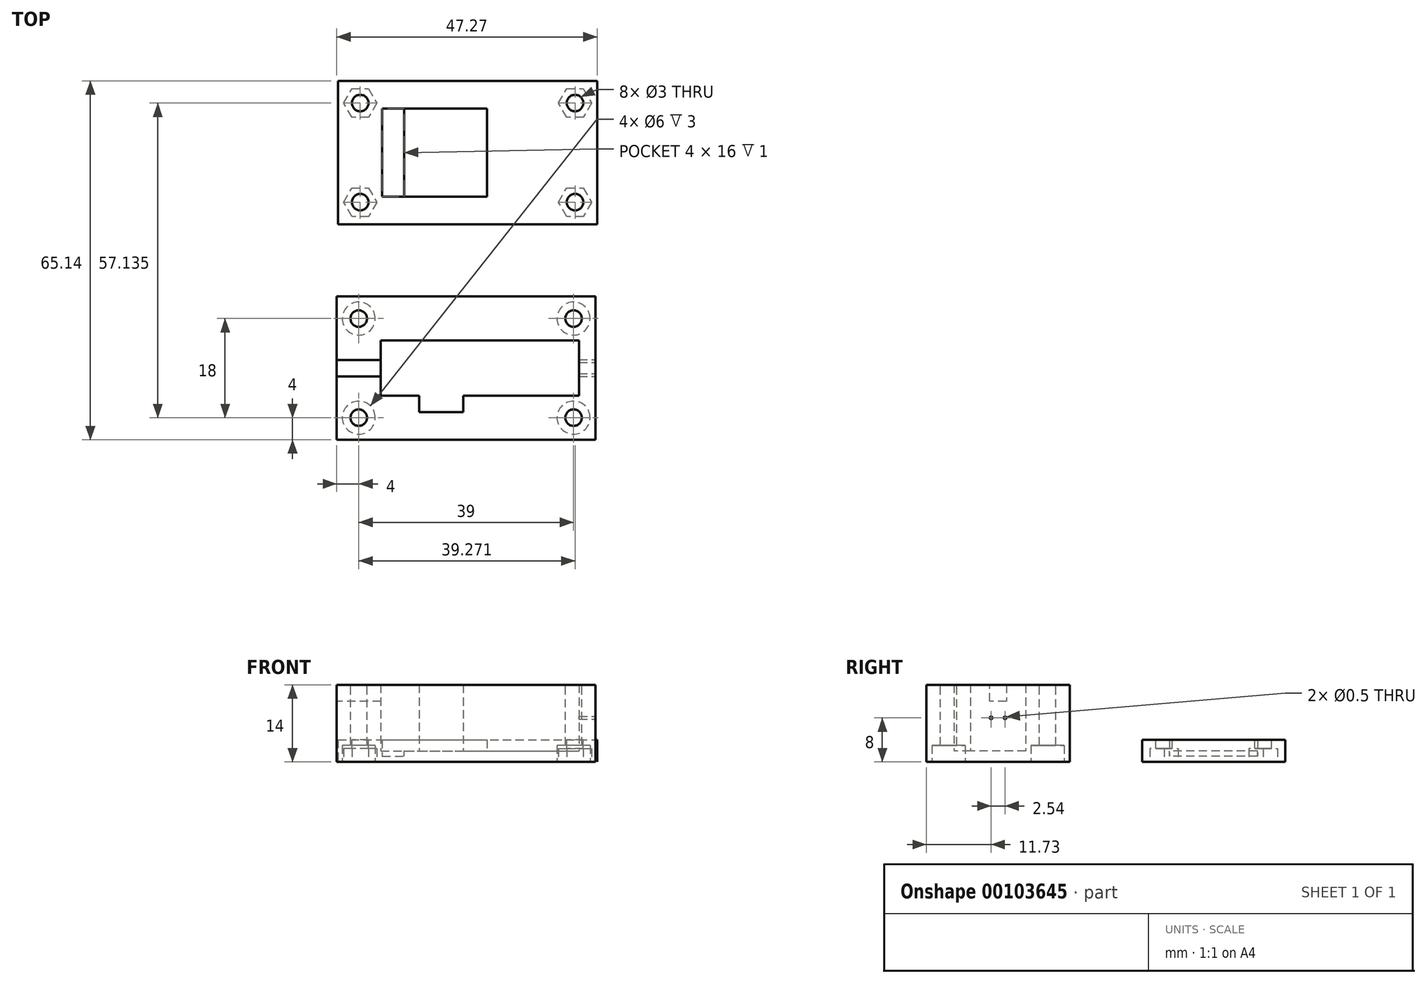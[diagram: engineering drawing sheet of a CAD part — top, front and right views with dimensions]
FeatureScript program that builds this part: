
annotation { "Feature Type Name" : "Feature", "Feature Type Description" : "" }
export const myFeature = defineFeature(function(context is Context, id is Id, definition is map)
    precondition{}
    {
        {
            var Q0;
            Q0=qCreatedBy(makeId("Top.planeOp"),FACE);
            var sketch = newSketch(context, id + "F0", { "sketchPlane" : qUnion([Q0])});
            skLineSegment(sketch, "E0.bottom", {"start": v(-10.35, 7.99) * mm, "end": v(8.65, 7.99) * mm});
            skLineSegment(sketch, "E0.top", {"start": v(-10.35, -8.01) * mm, "end": v(8.65, -8.01) * mm});
            skLineSegment(sketch, "E0.left", {"start": v(-10.35, 7.99) * mm, "end": v(-10.35, -8.01) * mm});
            skLineSegment(sketch, "E0.right", {"start": v(8.65, 7.99) * mm, "end": v(8.65, -8.01) * mm});
            skLineSegment(sketch, "E1.bottom", {"start": v(8.65, 7.99) * mm, "end": v(28.65, 7.99) * mm});
            skLineSegment(sketch, "E1.top", {"start": v(8.65, -8.01) * mm, "end": v(28.65, -8.01) * mm});
            skLineSegment(sketch, "E1.right", {"start": v(28.65, 7.99) * mm, "end": v(28.65, -8.01) * mm});
            skLineSegment(sketch, "E2.bottom", {"start": v(-10.35, 7.99) * mm, "end": v(28.65, 7.99) * mm});
            skLineSegment(sketch, "E2.top", {"start": v(-10.35, 12.99) * mm, "end": v(28.65, 12.99) * mm});
            skLineSegment(sketch, "E2.left", {"start": v(-10.35, 7.99) * mm, "end": v(-10.35, 12.99) * mm});
            skLineSegment(sketch, "E2.right", {"start": v(28.65, 7.99) * mm, "end": v(28.65, 12.99) * mm});
            skLineSegment(sketch, "E3.bottom", {"start": v(-10.35, -8.01) * mm, "end": v(28.65, -8.01) * mm});
            skLineSegment(sketch, "E3.top", {"start": v(-10.35, -13.01) * mm, "end": v(28.65, -13.01) * mm});
            skLineSegment(sketch, "E3.left", {"start": v(-10.35, -8.01) * mm, "end": v(-10.35, -13.01) * mm});
            skLineSegment(sketch, "E3.right", {"start": v(28.65, -8.01) * mm, "end": v(28.65, -13.01) * mm});
            skLineSegment(sketch, "E4.bottom", {"start": v(-10.35, 12.99) * mm, "end": v(-18.35, 12.99) * mm});
            skLineSegment(sketch, "E4.top", {"start": v(-10.35, -13.01) * mm, "end": v(-18.35, -13.01) * mm});
            skLineSegment(sketch, "E4.left", {"start": v(-10.35, 12.99) * mm, "end": v(-10.35, -13.01) * mm});
            skLineSegment(sketch, "E4.right", {"start": v(-18.35, 12.99) * mm, "end": v(-18.35, -13.01) * mm});
            skSolve(sketch);
        }
        {
            var Q0;
            {var subQ0=sQuery(id+"F0.wireOp",EDGE,"E0.right");Q0=makeQuery(id+"F0.imprint","IMPRINT",FACE,{"disambiguationData":[TD([[makeQuery(id+"F0.imprint","IMPRINT",EDGE,{"derivedFrom":subQ0}),-1.0]])]});}
            extrude(context, id + "F1", {"entities" : qUnion([Q0]), "depth" : 2 * mm});
        }
        {
            var Q0;
            Q0 = qSketchRegion(id + "F0", true);
            extrude(context, id + "F2", {"entities" : qUnion([Q0]), "operationType" : NewBodyOperationType.ADD, "depth" : 4 * mm});
        }
        {
            var Q0;
            Q0=qCreatedBy(makeId("Top.planeOp"),FACE);
            var sketch = newSketch(context, id + "F3", { "sketchPlane" : qUnion([Q0])});
            skLineSegment(sketch, "E5.bottom", {"start": v(-10.62, -31.15) * mm, "end": v(8.38, -31.15) * mm, "construction": true});
            skLineSegment(sketch, "E5.top", {"start": v(-10.62, -47.15) * mm, "end": v(8.38, -47.15) * mm, "construction": true});
            skLineSegment(sketch, "E5.left", {"start": v(-10.62, -31.15) * mm, "end": v(-10.62, -47.15) * mm, "construction": true});
            skLineSegment(sketch, "E5.right", {"start": v(8.38, -31.15) * mm, "end": v(8.38, -47.15) * mm, "construction": true});
            skLineSegment(sketch, "E6.top", {"start": v(-10.62, -26.15) * mm, "end": v(8.38, -26.15) * mm, "construction": true});
            skLineSegment(sketch, "E6.left", {"start": v(-10.62, -31.15) * mm, "end": v(-10.62, -26.15) * mm, "construction": true});
            skLineSegment(sketch, "E6.right", {"start": v(8.38, -31.15) * mm, "end": v(8.38, -26.15) * mm, "construction": true});
            skLineSegment(sketch, "E7.top", {"start": v(-10.62, -52.15) * mm, "end": v(8.38, -52.15) * mm, "construction": true});
            skLineSegment(sketch, "E7.left", {"start": v(-10.62, -47.15) * mm, "end": v(-10.62, -52.15) * mm, "construction": true});
            skLineSegment(sketch, "E7.right", {"start": v(8.38, -47.15) * mm, "end": v(8.38, -52.15) * mm, "construction": true});
            skLineSegment(sketch, "E8.bottom", {"start": v(-10.62, -26.15) * mm, "end": v(-18.62, -26.15) * mm, "construction": true});
            skLineSegment(sketch, "E8.top", {"start": v(-10.62, -52.15) * mm, "end": v(-18.62, -52.15) * mm, "construction": true});
            skLineSegment(sketch, "E8.left", {"start": v(-10.62, -26.15) * mm, "end": v(-10.62, -52.15) * mm, "construction": true});
            skLineSegment(sketch, "E8.right", {"start": v(-18.62, -26.15) * mm, "end": v(-18.62, -52.15) * mm, "construction": true});
            skLineSegment(sketch, "E9.bottom", {"start": v(8.38, -26.15) * mm, "end": v(28.38, -26.15) * mm, "construction": true});
            skLineSegment(sketch, "E9.top", {"start": v(8.38, -52.15) * mm, "end": v(28.38, -52.15) * mm, "construction": true});
            skLineSegment(sketch, "E9.left", {"start": v(8.38, -26.15) * mm, "end": v(8.38, -52.15) * mm, "construction": true});
            skLineSegment(sketch, "E9.right", {"start": v(28.38, -26.15) * mm, "end": v(28.38, -52.15) * mm, "construction": true});
            skLineSegment(sketch, "E10.bottom", {"start": v(-10.62, -44.15) * mm, "end": v(-3.62, -44.15) * mm, "construction": true});
            skLineSegment(sketch, "E10.top", {"start": v(-10.62, -47.15) * mm, "end": v(-3.62, -47.15) * mm, "construction": true});
            skLineSegment(sketch, "E10.left", {"start": v(-10.62, -44.15) * mm, "end": v(-10.62, -47.15) * mm, "construction": true});
            skLineSegment(sketch, "E10.right", {"start": v(-3.62, -44.15) * mm, "end": v(-3.62, -47.15) * mm, "construction": true});
            skLineSegment(sketch, "E11.bottom", {"start": v(8.38, -44.15) * mm, "end": v(4.38, -44.15) * mm, "construction": true});
            skLineSegment(sketch, "E11.top", {"start": v(8.38, -47.15) * mm, "end": v(4.38, -47.15) * mm, "construction": true});
            skLineSegment(sketch, "E11.left", {"start": v(8.38, -44.15) * mm, "end": v(8.38, -47.15) * mm, "construction": true});
            skLineSegment(sketch, "E11.right", {"start": v(4.38, -44.15) * mm, "end": v(4.38, -47.15) * mm, "construction": true});
            skLineSegment(sketch, "E12.top", {"start": v(-10.62, -34.15) * mm, "end": v(8.38, -34.15) * mm, "construction": true});
            skLineSegment(sketch, "E12.left", {"start": v(-10.62, -31.15) * mm, "end": v(-10.62, -34.15) * mm, "construction": true});
            skLineSegment(sketch, "E12.right", {"start": v(8.38, -31.15) * mm, "end": v(8.38, -34.15) * mm, "construction": true});
            skLineSegment(sketch, "E13.bottom", {"start": v(28.38, -26.15) * mm, "end": v(25.38, -26.15) * mm, "construction": true});
            skLineSegment(sketch, "E13.top", {"start": v(28.38, -52.15) * mm, "end": v(25.38, -52.15) * mm, "construction": true});
            skLineSegment(sketch, "E13.right", {"start": v(25.38, -26.15) * mm, "end": v(25.38, -52.15) * mm, "construction": true});
            skLineSegment(sketch, "E14", {"start": v(-10.62, -34.15) * mm, "end": v(25.38, -34.15) * mm});
            skLineSegment(sketch, "E15", {"start": v(-10.62, -34.15) * mm, "end": v(-10.62, -44.15) * mm});
            skLineSegment(sketch, "E16", {"start": v(-10.62, -44.15) * mm, "end": v(-3.62, -44.15) * mm});
            skLineSegment(sketch, "E17", {"start": v(-3.62, -47.15) * mm, "end": v(4.38, -47.15) * mm});
            skLineSegment(sketch, "E18", {"start": v(4.38, -44.15) * mm, "end": v(25.38, -44.15) * mm});
            skLineSegment(sketch, "E19", {"start": v(25.38, -44.15) * mm, "end": v(25.38, -34.15) * mm});
            skLineSegment(sketch, "E20.bottom", {"start": v(-18.62, -26.15) * mm, "end": v(28.38, -26.15) * mm});
            skLineSegment(sketch, "E20.top", {"start": v(-18.62, -52.15) * mm, "end": v(28.38, -52.15) * mm});
            skLineSegment(sketch, "E20.left", {"start": v(-18.62, -26.15) * mm, "end": v(-18.62, -52.15) * mm});
            skLineSegment(sketch, "E20.right", {"start": v(28.38, -26.15) * mm, "end": v(28.38, -52.15) * mm});
            skLineSegment(sketch, "E21", {"start": v(4.38, -47.15) * mm, "end": v(-3.62, -47.15) * mm});
            skLineSegment(sketch, "E22", {"start": v(-3.62, -44.15) * mm, "end": v(-3.62, -47.15) * mm});
            skLineSegment(sketch, "E23", {"start": v(4.38, -44.15) * mm, "end": v(4.38, -47.15) * mm});
            skSolve(sketch);
        }
        {
            var Q0;
            Q0=makeQuery(id+"F3.imprint","IMPRINT",FACE,{"disambiguationData":[TD([[makeQuery(id+"F3.imprint","IMPRINT",EDGE,{"derivedFrom":sQuery(id+"F3.wireOp",EDGE,"E14")}),1.0]])]});
            extrude(context, id + "F4", {"entities" : qUnion([Q0]), "depth" : 14 * mm});
        }
        {
            var Q0;
            Q0=makeQuery(id+"F3.imprint","IMPRINT",FACE,{"disambiguationData":[TD([[makeQuery(id+"F3.imprint","IMPRINT",EDGE,{"derivedFrom":sQuery(id+"F3.wireOp",EDGE,"E14")}),-1.0]])]});
            extrude(context, id + "F5", {"entities" : qUnion([Q0]), "operationType" : NewBodyOperationType.ADD, "depth" : 2 * mm});
        }
        {
            var Q0;
            Q0=makeQuery(id+"F4.opExtrude","SWEPT_FACE",FACE,{"disambiguationData":[OSD([sQuery(id+"F3.wireOp",EDGE,"E20.right")])]});
            var sketch = newSketch(context, id + "F6", { "sketchPlane" : qUnion([Q0])});
            skLineSegment(sketch, "E24", {"start": v(-26.15, 8) * mm, "end": v(-52.15, 8) * mm, "construction": true});
            skLineSegment(sketch, "E25", {"start": v(-39.15, 14) * mm, "end": v(-39.15, 0) * mm, "construction": true});
            skCircle(sketch, "E26", {"center": v(-37.88, 8) * mm, "radius": 0.25 * mm});
            skCircle(sketch, "E27", {"center": v(-40.42, 8) * mm, "radius": 0.25 * mm});
            skSolve(sketch);
        }
        {
            var Q0;
            Q0 = qSketchRegion(id + "F6", true);
            extrude(context, id + "F7", {"entities" : qUnion([Q0]), "operationType" : NewBodyOperationType.REMOVE, "oppositeDirection" : true, "depth" : 5 * mm});
        }
        {
            var Q0;
            Q0=makeQuery(id+"F4.opExtrude","SWEPT_FACE",FACE,{"disambiguationData":[OSD([sQuery(id+"F3.wireOp",EDGE,"E20.left")])]});
            var sketch = newSketch(context, id + "F8", { "sketchPlane" : qUnion([Q0])});
            skLineSegment(sketch, "E28", {"start": v(39.15, 14) * mm, "end": v(39.15, 0) * mm, "construction": true});
            skLineSegment(sketch, "E29.bottom", {"start": v(37.65, 14) * mm, "end": v(39.15, 14) * mm});
            skLineSegment(sketch, "E29.top", {"start": v(37.65, 11) * mm, "end": v(39.15, 11) * mm});
            skLineSegment(sketch, "E29.left", {"start": v(37.65, 14) * mm, "end": v(37.65, 11) * mm});
            skLineSegment(sketch, "E29.right", {"start": v(39.15, 14) * mm, "end": v(39.15, 11) * mm});
            skLineSegment(sketch, "E30.bottom", {"start": v(39.15, 11) * mm, "end": v(40.65, 11) * mm});
            skLineSegment(sketch, "E30.top", {"start": v(39.15, 14) * mm, "end": v(40.65, 14) * mm});
            skLineSegment(sketch, "E30.left", {"start": v(39.15, 11) * mm, "end": v(39.15, 14) * mm});
            skLineSegment(sketch, "E30.right", {"start": v(40.65, 11) * mm, "end": v(40.65, 14) * mm});
            skSolve(sketch);
        }
        {
            var Q0;
            Q0=makeQuery(id+"F8.imprint","IMPRINT",FACE,{"disambiguationData":[TD([[makeQuery(id+"F8.imprint","IMPRINT",EDGE,{"derivedFrom":sQuery(id+"F8.wireOp",EDGE,"E29.bottom")}),-1.0]])]});
            var Q1;
            Q1=makeQuery(id+"F8.imprint","IMPRINT",FACE,{"disambiguationData":[TD([[makeQuery(id+"F8.imprint","IMPRINT",EDGE,{"derivedFrom":sQuery(id+"F8.wireOp",EDGE,"E30.bottom")}),1.0]])]});
            extrude(context, id + "F9", {"entities" : qUnion([Q0, Q1]), "operationType" : NewBodyOperationType.REMOVE, "oppositeDirection" : true, "depth" : 8 * mm});
        }
        {
            var Q0;
            Q0=makeQuery(id+"F2.opExtrude","CAP_FACE",FACE,{"disambiguationData":[OSD([sQuery(id+"F0.wireOp",EDGE,"E0.right"),sQuery(id+"F0.wireOp",EDGE,"E1.right"),sQuery(id+"F0.wireOp",EDGE,"E2.bottom"),sQuery(id+"F0.wireOp",EDGE,"E2.top"),sQuery(id+"F0.wireOp",EDGE,"E2.right"),sQuery(id+"F0.wireOp",EDGE,"E3.bottom"),sQuery(id+"F0.wireOp",EDGE,"E3.top"),sQuery(id+"F0.wireOp",EDGE,"E3.right"),sQuery(id+"F0.wireOp",EDGE,"E4.bottom"),sQuery(id+"F0.wireOp",EDGE,"E4.top"),sQuery(id+"F0.wireOp",EDGE,"E4.left"),sQuery(id+"F0.wireOp",EDGE,"E4.right")])],"isStart":false});
            var sketch = newSketch(context, id + "F10", { "sketchPlane" : qUnion([Q0])});
            skLineSegment(sketch, "E31", {"start": v(28.65, 8.99) * mm, "end": v(-18.35, 8.99) * mm, "construction": true});
            skLineSegment(sketch, "E32", {"start": v(28.65, -9.01) * mm, "end": v(-18.35, -9.01) * mm, "construction": true});
            skLineSegment(sketch, "E33", {"start": v(-14.35, 12.99) * mm, "end": v(-14.35, -13.01) * mm, "construction": true});
            skLineSegment(sketch, "E34", {"start": v(24.65, 12.99) * mm, "end": v(24.65, -13.01) * mm, "construction": true});
            skCircle(sketch, "E35", {"center": v(-14.35, 8.99) * mm, "radius": 1.5 * mm});
            skCircle(sketch, "E36", {"center": v(24.65, 8.99) * mm, "radius": 1.5 * mm});
            skCircle(sketch, "E37", {"center": v(24.65, -9.01) * mm, "radius": 1.5 * mm});
            skCircle(sketch, "E38", {"center": v(-14.35, -9.01) * mm, "radius": 1.5 * mm});
            skSolve(sketch);
        }
        {
            var Q0;
            Q0 = qSketchRegion(id + "F10", true);
            extrude(context, id + "F11", {"entities" : qUnion([Q0]), "operationType" : NewBodyOperationType.REMOVE, "oppositeDirection" : true, "depth" : 4 * mm});
        }
        {
            var Q0;
            Q0=makeQuery(id+"F4.opExtrude","CAP_FACE",FACE,{"disambiguationData":[OSD([sQuery(id+"F3.wireOp",EDGE,"E14"),sQuery(id+"F3.wireOp",EDGE,"E15"),sQuery(id+"F3.wireOp",EDGE,"E16"),sQuery(id+"F3.wireOp",EDGE,"E18"),sQuery(id+"F3.wireOp",EDGE,"E20.bottom"),sQuery(id+"F3.wireOp",EDGE,"E20.top"),sQuery(id+"F3.wireOp",EDGE,"E20.left"),sQuery(id+"F3.wireOp",EDGE,"E20.right"),sQuery(id+"F3.wireOp",EDGE,"E22"),sQuery(id+"F3.wireOp",EDGE,"E23"),sQuery(id+"F3.wireOp",EDGE,"E17"),sQuery(id+"F3.wireOp",EDGE,"E19")])],"isStart":false});
            var sketch = newSketch(context, id + "F12", { "sketchPlane" : qUnion([Q0])});
            skLineSegment(sketch, "E39", {"start": v(-18.62, -30.15) * mm, "end": v(28.38, -30.15) * mm, "construction": true});
            skLineSegment(sketch, "E40", {"start": v(-18.62, -48.15) * mm, "end": v(28.38, -48.15) * mm, "construction": true});
            skLineSegment(sketch, "E41", {"start": v(-14.62, -26.15) * mm, "end": v(-14.62, -52.15) * mm, "construction": true});
            skLineSegment(sketch, "E42", {"start": v(24.38, -26.15) * mm, "end": v(24.38, -52.15) * mm, "construction": true});
            skCircle(sketch, "E43", {"center": v(-14.62, -30.15) * mm, "radius": 1.5 * mm});
            skCircle(sketch, "E44", {"center": v(24.38, -30.15) * mm, "radius": 1.5 * mm});
            skCircle(sketch, "E45", {"center": v(24.38, -48.15) * mm, "radius": 1.5 * mm});
            skCircle(sketch, "E46", {"center": v(-14.62, -48.15) * mm, "radius": 1.5 * mm});
            skSolve(sketch);
        }
        {
            var Q0;
            Q0 = qSketchRegion(id + "F12", true);
            extrude(context, id + "F13", {"entities" : qUnion([Q0]), "operationType" : NewBodyOperationType.REMOVE, "oppositeDirection" : true, "depth" : 25 * mm});
        }
        {
            var Q0;
            Q0=makeQuery(id+"F1.opExtrude","CAP_FACE",FACE,{"disambiguationData":[OSD([sQuery(id+"F0.wireOp",EDGE,"E0.right"),sQuery(id+"F0.wireOp",EDGE,"E2.bottom"),sQuery(id+"F0.wireOp",EDGE,"E3.bottom"),sQuery(id+"F0.wireOp",EDGE,"E4.left")])],"isStart":false});
            var sketch = newSketch(context, id + "F14", { "sketchPlane" : qUnion([Q0])});
            skLineSegment(sketch, "E47.bottom", {"start": v(-10.35, 7.99) * mm, "end": v(-6.35, 7.99) * mm});
            skLineSegment(sketch, "E47.top", {"start": v(-10.35, -8.01) * mm, "end": v(-6.35, -8.01) * mm});
            skLineSegment(sketch, "E47.left", {"start": v(-10.35, 7.99) * mm, "end": v(-10.35, -8.01) * mm});
            skLineSegment(sketch, "E47.right", {"start": v(-6.35, 7.99) * mm, "end": v(-6.35, -8.01) * mm});
            skSolve(sketch);
        }
        {
            var Q0;
            Q0=makeQuery(id+"F14.imprint","IMPRINT",FACE,{"disambiguationData":[TD([[makeQuery(id+"F14.imprint","IMPRINT",EDGE,{"derivedFrom":sQuery(id+"F14.wireOp",EDGE,"E47.bottom")}),-1.0]])]});
            extrude(context, id + "F15", {"entities" : qUnion([Q0]), "operationType" : NewBodyOperationType.REMOVE, "oppositeDirection" : true, "depth" : 1 * mm});
        }
        {
            var Q0;
            Q0=makeQuery(id+"F3.imprint","IMPRINT",FACE,{"disambiguationData":[TD([[makeQuery(id+"F3.imprint","IMPRINT",EDGE,{"derivedFrom":sQuery(id+"F3.wireOp",EDGE,"E14")}),1.0]])]});
            var sketch = newSketch(context, id + "F16", { "sketchPlane" : qUnion([Q0])});
            skLineSegment(sketch, "E48.bottom", {"start": v(24.38, -30.15) * mm, "end": v(-14.62, -30.15) * mm, "construction": true});
            skLineSegment(sketch, "E48.top", {"start": v(24.38, -48.15) * mm, "end": v(-14.62, -48.15) * mm, "construction": true});
            skLineSegment(sketch, "E48.left", {"start": v(24.38, -30.15) * mm, "end": v(24.38, -48.15) * mm, "construction": true});
            skLineSegment(sketch, "E48.right", {"start": v(-14.62, -30.15) * mm, "end": v(-14.62, -48.15) * mm, "construction": true});
            skCircle(sketch, "E49", {"center": v(24.38, -30.15) * mm, "radius": 3 * mm});
            skCircle(sketch, "E50", {"center": v(-14.62, -30.15) * mm, "radius": 3 * mm});
            skCircle(sketch, "E51", {"center": v(24.38, -48.15) * mm, "radius": 3 * mm});
            skCircle(sketch, "E52", {"center": v(-14.62, -48.15) * mm, "radius": 3 * mm});
            skSolve(sketch);
        }
        {
            var Q0;
            Q0 = qSketchRegion(id + "F16", true);
            extrude(context, id + "F17", {"entities" : qUnion([Q0]), "operationType" : NewBodyOperationType.REMOVE, "depth" : 3 * mm});
        }
        {
            var Q0;
            {var subQ3=sQuery(id+"F0.wireOp",EDGE,"E4.bottom");Q0=makeQuery(id+"F0.imprint","IMPRINT",FACE,{"disambiguationData":[TD([[makeQuery(id+"F0.imprint","IMPRINT",EDGE,{"derivedFrom":subQ3}),1.0]])]});}
            var sketch = newSketch(context, id + "F18", { "sketchPlane" : qUnion([Q0])});
            skLineSegment(sketch, "E53.bottom", {"start": v(-14.35, -9.01) * mm, "end": v(24.65, -9.01) * mm, "construction": true});
            skLineSegment(sketch, "E53.top", {"start": v(-14.35, 8.99) * mm, "end": v(24.65, 8.99) * mm, "construction": true});
            skLineSegment(sketch, "E53.left", {"start": v(-14.35, -9.01) * mm, "end": v(-14.35, 8.99) * mm, "construction": true});
            skLineSegment(sketch, "E53.right", {"start": v(24.65, -9.01) * mm, "end": v(24.65, 8.99) * mm, "construction": true});
            skCircle(sketch, "E54.cCircle", {"center": v(24.65, -9.01) * mm, "radius": 3 * mm, "construction": true});
            skLineSegment(sketch, "E54.0", {"start": v(21.65, -9.01) * mm, "end": v(23.15, -6.42) * mm});
            skLineSegment(sketch, "E54.1", {"start": v(23.15, -6.42) * mm, "end": v(26.15, -6.42) * mm});
            skLineSegment(sketch, "E54.2", {"start": v(26.15, -6.42) * mm, "end": v(27.65, -9.01) * mm});
            skLineSegment(sketch, "E54.3", {"start": v(27.65, -9.01) * mm, "end": v(26.15, -11.61) * mm});
            skLineSegment(sketch, "E54.4", {"start": v(26.15, -11.61) * mm, "end": v(23.15, -11.61) * mm});
            skLineSegment(sketch, "E54.5", {"start": v(23.15, -11.61) * mm, "end": v(21.65, -9.01) * mm});
            skCircle(sketch, "E55.cCircle", {"center": v(-14.35, -9.01) * mm, "radius": 3 * mm, "construction": true});
            skLineSegment(sketch, "E55.0", {"start": v(-11.35, -9.01) * mm, "end": v(-12.85, -11.61) * mm});
            skLineSegment(sketch, "E55.1", {"start": v(-12.85, -11.61) * mm, "end": v(-15.85, -11.61) * mm});
            skLineSegment(sketch, "E55.2", {"start": v(-15.85, -11.61) * mm, "end": v(-17.35, -9.01) * mm});
            skLineSegment(sketch, "E55.3", {"start": v(-17.35, -9.01) * mm, "end": v(-15.85, -6.42) * mm});
            skLineSegment(sketch, "E55.4", {"start": v(-15.85, -6.42) * mm, "end": v(-12.85, -6.42) * mm});
            skLineSegment(sketch, "E55.5", {"start": v(-12.85, -6.42) * mm, "end": v(-11.35, -9.01) * mm});
            skCircle(sketch, "E56.cCircle", {"center": v(-14.35, 8.99) * mm, "radius": 3 * mm, "construction": true});
            skLineSegment(sketch, "E56.0", {"start": v(-11.35, 8.99) * mm, "end": v(-12.85, 6.39) * mm});
            skLineSegment(sketch, "E56.1", {"start": v(-12.85, 6.39) * mm, "end": v(-15.85, 6.39) * mm});
            skLineSegment(sketch, "E56.2", {"start": v(-15.85, 6.39) * mm, "end": v(-17.35, 8.99) * mm});
            skLineSegment(sketch, "E56.3", {"start": v(-17.35, 8.99) * mm, "end": v(-15.85, 11.58) * mm});
            skLineSegment(sketch, "E56.4", {"start": v(-15.85, 11.58) * mm, "end": v(-12.85, 11.58) * mm});
            skLineSegment(sketch, "E56.5", {"start": v(-12.85, 11.58) * mm, "end": v(-11.35, 8.99) * mm});
            skCircle(sketch, "E57.cCircle", {"center": v(24.65, 8.99) * mm, "radius": 3 * mm, "construction": true});
            skLineSegment(sketch, "E57.0", {"start": v(21.65, 8.99) * mm, "end": v(23.15, 11.58) * mm});
            skLineSegment(sketch, "E57.1", {"start": v(23.15, 11.58) * mm, "end": v(26.15, 11.58) * mm});
            skLineSegment(sketch, "E57.2", {"start": v(26.15, 11.58) * mm, "end": v(27.65, 8.99) * mm});
            skLineSegment(sketch, "E57.3", {"start": v(27.65, 8.99) * mm, "end": v(26.15, 6.39) * mm});
            skLineSegment(sketch, "E57.4", {"start": v(26.15, 6.39) * mm, "end": v(23.15, 6.39) * mm});
            skLineSegment(sketch, "E57.5", {"start": v(23.15, 6.39) * mm, "end": v(21.65, 8.99) * mm});
            skSolve(sketch);
        }
        {
            var Q0;
            Q0 = qSketchRegion(id + "F18", true);
            extrude(context, id + "F19", {"entities" : qUnion([Q0]), "operationType" : NewBodyOperationType.REMOVE, "depth" : 2.4 * mm});
        }
    });
